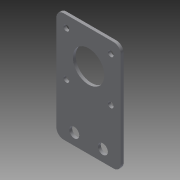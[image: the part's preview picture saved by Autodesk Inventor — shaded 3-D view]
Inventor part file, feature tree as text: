
AUTODESK INVENTOR PART (.ipt)
format: ipt  version: 2015 SP1 (Build 190203100, 203)  size: 113,664 bytes
history: native  units: in
note: dims shown in document units (in); Inventor stores cm internally (conversion verified against a paired STEP export)
features: extrude x1
ambient origin geometry x8: Origin, YZ Plane, XZ Plane, XY Plane, X Axis, Y Axis, Z Axis, Center Point
bodies: Body1 (feature_tree)
feature tree (1):
  extrude  "Extrusion4"  Depth=0.8661in
